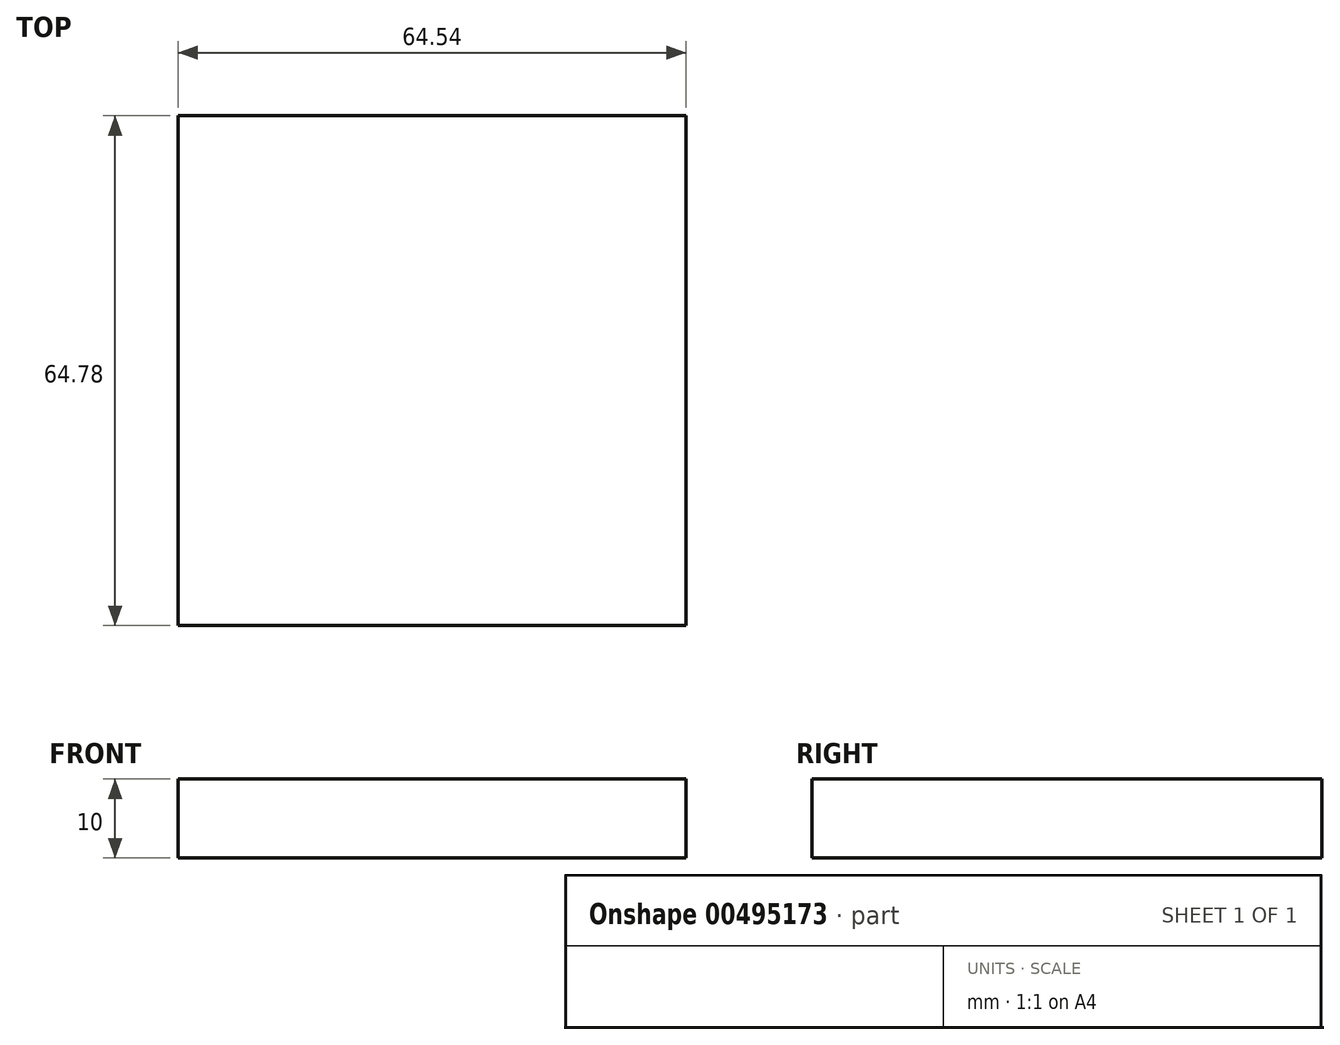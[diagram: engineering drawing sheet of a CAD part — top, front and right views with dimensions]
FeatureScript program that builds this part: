
annotation { "Feature Type Name" : "Feature", "Feature Type Description" : "" }
export const myFeature = defineFeature(function(context is Context, id is Id, definition is map)
    precondition{}
    {
        {
            var Q0;
            Q0=qCreatedBy(makeId("Top.planeOp"),FACE);
            var sketch = newSketch(context, id + "F0", { "sketchPlane" : qUnion([Q0])});
            skLineSegment(sketch, "E0.bottom", {"start": v(28.06, 44.4) * mm, "end": v(-36.48, 44.4) * mm});
            skLineSegment(sketch, "E0.top", {"start": v(28.06, -20.37) * mm, "end": v(-36.48, -20.37) * mm});
            skLineSegment(sketch, "E0.left", {"start": v(28.06, 44.4) * mm, "end": v(28.06, -20.37) * mm});
            skLineSegment(sketch, "E0.right", {"start": v(-36.48, 44.4) * mm, "end": v(-36.48, -20.37) * mm});
            skSolve(sketch);
        }
        {
            var Q0;
            Q0=makeQuery(id+"F0.imprint","IMPRINT",FACE,{"disambiguationData":[TD([[makeQuery(id+"F0.imprint","IMPRINT",EDGE,{"derivedFrom":sQuery(id+"F0.wireOp",EDGE,"E0.bottom")}),1.0]])]});
            extrude(context, id + "F1", {"entities" : qUnion([Q0]), "depth" : 10 * mm});
        }
    });
